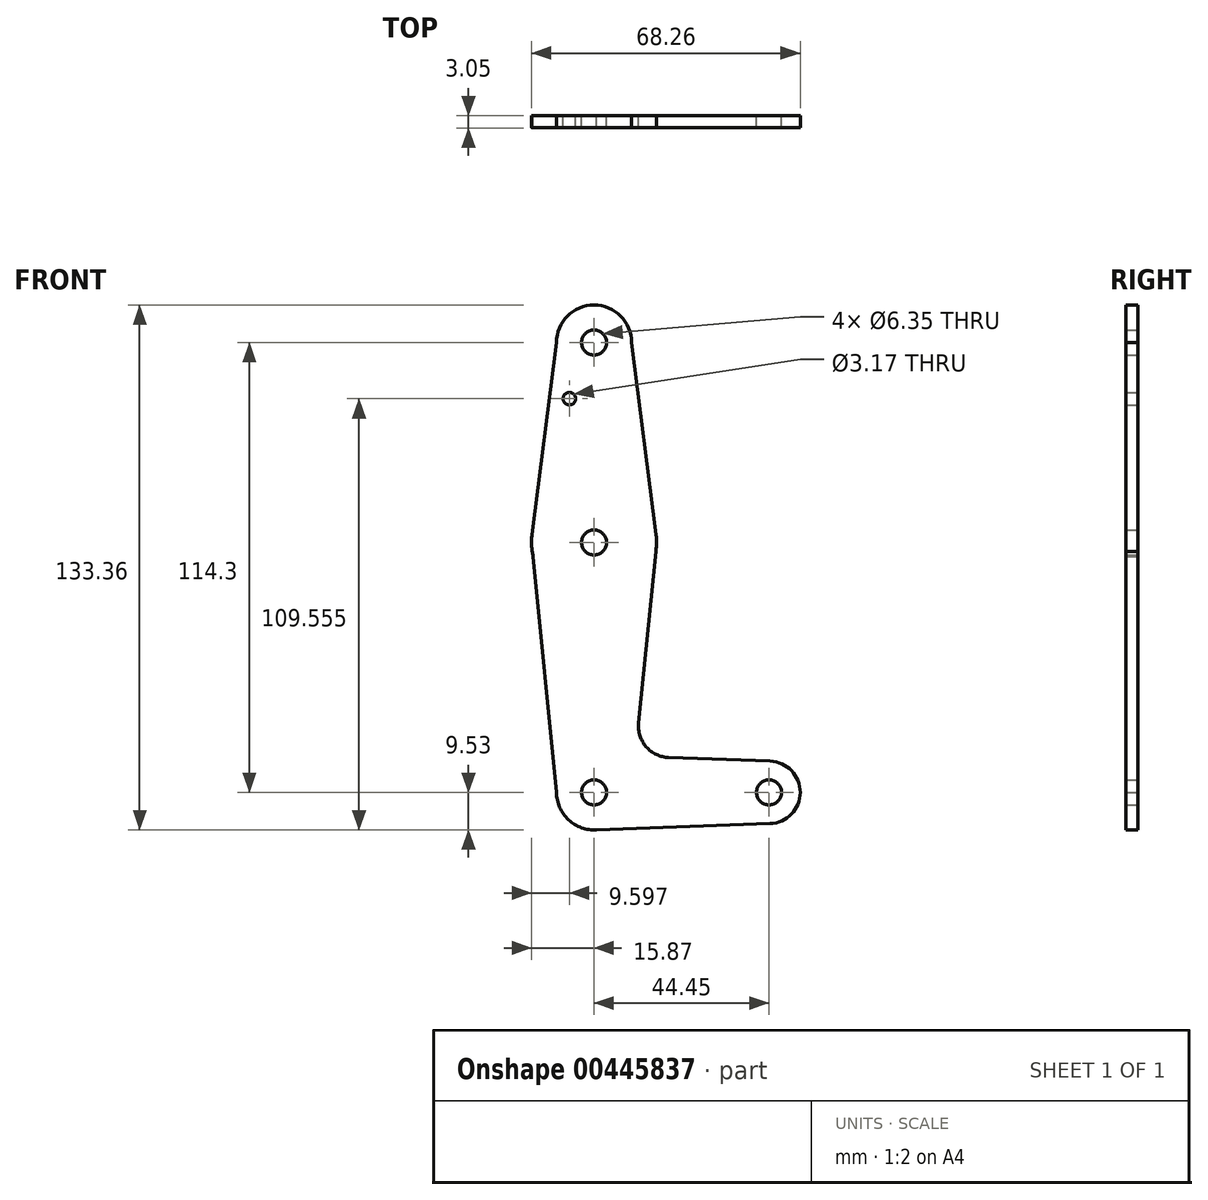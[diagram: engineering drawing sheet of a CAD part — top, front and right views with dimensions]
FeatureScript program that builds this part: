
annotation { "Feature Type Name" : "Feature", "Feature Type Description" : "" }
export const myFeature = defineFeature(function(context is Context, id is Id, definition is map)
    precondition{}
    {
        {
            var Q0;
            Q0=qCreatedBy(makeId("Front.planeOp"),FACE);
            var sketch = newSketch(context, id + "F0", { "sketchPlane" : qUnion([Q0])});
            skLineSegment(sketch, "E0", {"start": v(0, 0) * mm, "end": v(0, 114.3) * mm, "construction": true});
            skLineSegment(sketch, "E1", {"start": v(0, 0) * mm, "end": v(44.45, 0) * mm, "construction": true});
            skCircle(sketch, "E2", {"center": v(0, 114.3) * mm, "radius": 9.53 * mm});
            skCircle(sketch, "E3", {"center": v(0, 0) * mm, "radius": 9.53 * mm});
            skCircle(sketch, "E4", {"center": v(0, 63.5) * mm, "radius": 15.88 * mm});
            skCircle(sketch, "E5", {"center": v(44.45, 0) * mm, "radius": 7.94 * mm});
            skLineSegment(sketch, "E6", {"start": v(9.53, 114.3) * mm, "end": v(15.75, 65.5) * mm});
            skLineSegment(sketch, "E7", {"start": v(-9.53, 114.3) * mm, "end": v(-15.75, 65.5) * mm});
            skLineSegment(sketch, "E8", {"start": v(18.96, 8.85) * mm, "end": v(44.73, 7.93) * mm});
            skLineSegment(sketch, "E9", {"start": v(0, -9.53) * mm, "end": v(44.73, -7.93) * mm});
            skLineSegment(sketch, "E10", {"start": v(-15.47, 59.95) * mm, "end": v(-9.52, 0) * mm});
            skLineSegment(sketch, "E11", {"start": v(15.7, 61.2) * mm, "end": v(11.34, 17.59) * mm});
            skCircle(sketch, "E12", {"center": v(0, 114.3) * mm, "radius": 3.18 * mm});
            skCircle(sketch, "E13", {"center": v(0, 63.5) * mm, "radius": 3.18 * mm});
            skCircle(sketch, "E14", {"center": v(0, 0) * mm, "radius": 3.18 * mm});
            skCircle(sketch, "E15", {"center": v(44.45, 0) * mm, "radius": 3.18 * mm});
            skArc(sketch, "E16.filletArc", {"start": v(11.34, 17.59) * mm, "mid": v(13.26, 11.57) * mm, "end": v(18.96, 8.85) * mm});
            skCircle(sketch, "E17", {"center": v(-6.27, 100.03) * mm, "radius": 1.59 * mm});
            skSolve(sketch);
        }
        {
            var Q0;
            Q0 = qSketchRegion(id + "F0", true);
            extrude(context, id + "F1", {"entities" : qUnion([Q0]), "depth" : 3.05 * mm});
        }
    });
